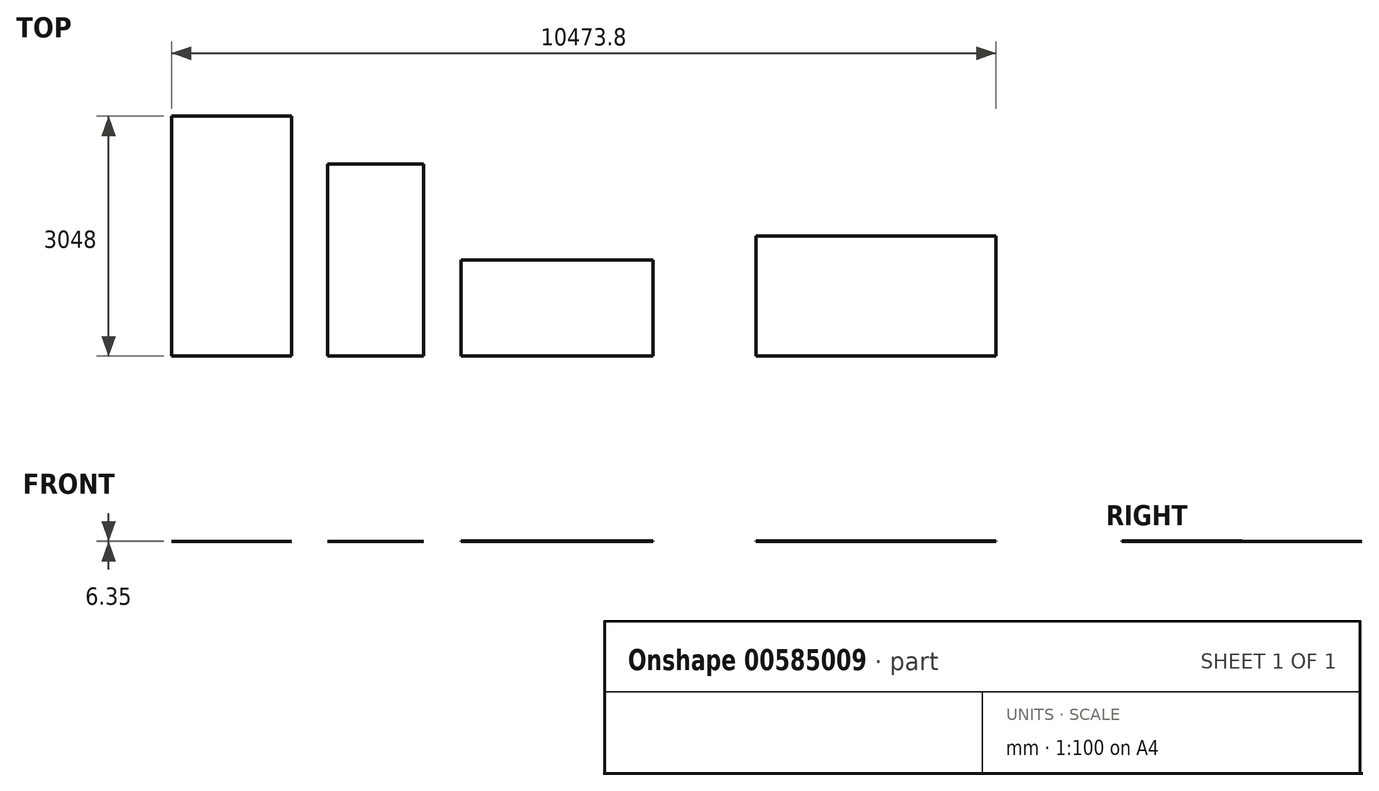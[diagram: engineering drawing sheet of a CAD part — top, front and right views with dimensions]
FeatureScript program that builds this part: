
annotation { "Feature Type Name" : "Feature", "Feature Type Description" : "" }
export const myFeature = defineFeature(function(context is Context, id is Id, definition is map)
    precondition{}
    {
        {
            var Q0;
            Q0=qCreatedBy(makeId("Top.planeOp"), FACE);
            var sketch = newSketch(context, id + "F0", { "sketchPlane" : qUnion([Q0])});
            skLineSegment(sketch, "E0.bottom", {"start": v(0, 0) * mm, "end": v(1219.2, 0) * mm});
            skLineSegment(sketch, "E0.top", {"start": v(0, 2438.4) * mm, "end": v(1219.2, 2438.4) * mm});
            skLineSegment(sketch, "E0.left", {"start": v(0, 0) * mm, "end": v(0, 2438.4) * mm});
            skLineSegment(sketch, "E0.right", {"start": v(1219.2, 0) * mm, "end": v(1219.2, 2438.4) * mm});
            skSolve(sketch);
        }
        {
            var Q0;
            Q0 = qSketchRegion(id + "F0", true);
            extrude(context, id + "F1", {"entities" : qUnion([Q0]), "depth" : 3.17 * mm, "offsetDistance" : 25.4 * mm});
        }
        {
            var Q0;
            Q0=qCreatedBy(makeId("Top.planeOp"), FACE);
            var sketch = newSketch(context, id + "F2", { "sketchPlane" : qUnion([Q0])});
            skLineSegment(sketch, "E1.bottom", {"start": v(-459.47, 0) * mm, "end": v(-1983.47, 0) * mm});
            skLineSegment(sketch, "E1.top", {"start": v(-459.47, 3048) * mm, "end": v(-1983.47, 3048) * mm});
            skLineSegment(sketch, "E1.left", {"start": v(-459.47, 0) * mm, "end": v(-459.47, 3048) * mm});
            skLineSegment(sketch, "E1.right", {"start": v(-1983.47, 0) * mm, "end": v(-1983.47, 3048) * mm});
            skSolve(sketch);
        }
        {
            var Q0;
            Q0 = qSketchRegion(id + "F2", true);
            extrude(context, id + "F3", {"entities" : qUnion([Q0]), "depth" : 3.17 * mm, "offsetDistance" : 25.4 * mm});
        }
        {
            var Q0;
            Q0=qCreatedBy(makeId("Top.planeOp"), FACE);
            var sketch = newSketch(context, id + "F4", { "sketchPlane" : qUnion([Q0])});
            skLineSegment(sketch, "E2.bottom", {"start": v(1691.82, 0) * mm, "end": v(4130.22, 0) * mm});
            skLineSegment(sketch, "E2.top", {"start": v(1691.82, 1219.2) * mm, "end": v(4130.22, 1219.2) * mm});
            skLineSegment(sketch, "E2.left", {"start": v(1691.82, 0) * mm, "end": v(1691.82, 1219.2) * mm});
            skLineSegment(sketch, "E2.right", {"start": v(4130.22, 0) * mm, "end": v(4130.22, 1219.2) * mm});
            skSolve(sketch);
        }
        {
            var Q0;
            Q0 = qSketchRegion(id + "F4", true);
            extrude(context, id + "F5", {"entities" : qUnion([Q0]), "domain" : OperationDomain.MODEL, "flatOperationType" : FlatOperationType.REMOVE, "depth" : 6.35 * mm, "offsetDistance" : 25.4 * mm});
        }
        {
            var Q0;
            Q0=qCreatedBy(makeId("Top.planeOp"), FACE);
            var sketch = newSketch(context, id + "F6", { "sketchPlane" : qUnion([Q0])});
            skLineSegment(sketch, "E3.bottom", {"start": v(5442.36, 1524) * mm, "end": v(8490.36, 1524) * mm});
            skLineSegment(sketch, "E3.top", {"start": v(5442.36, 0) * mm, "end": v(8490.36, 0) * mm});
            skLineSegment(sketch, "E3.left", {"start": v(5442.36, 1524) * mm, "end": v(5442.36, 0) * mm});
            skLineSegment(sketch, "E3.right", {"start": v(8490.36, 1524) * mm, "end": v(8490.36, 0) * mm});
            skSolve(sketch);
        }
        {
            var Q0;
            Q0 = qSketchRegion(id + "F6", true);
            extrude(context, id + "F7", {"entities" : qUnion([Q0]), "domain" : OperationDomain.MODEL, "flatOperationType" : FlatOperationType.REMOVE, "depth" : 6.35 * mm, "offsetDistance" : 25.4 * mm});
        }
    });
